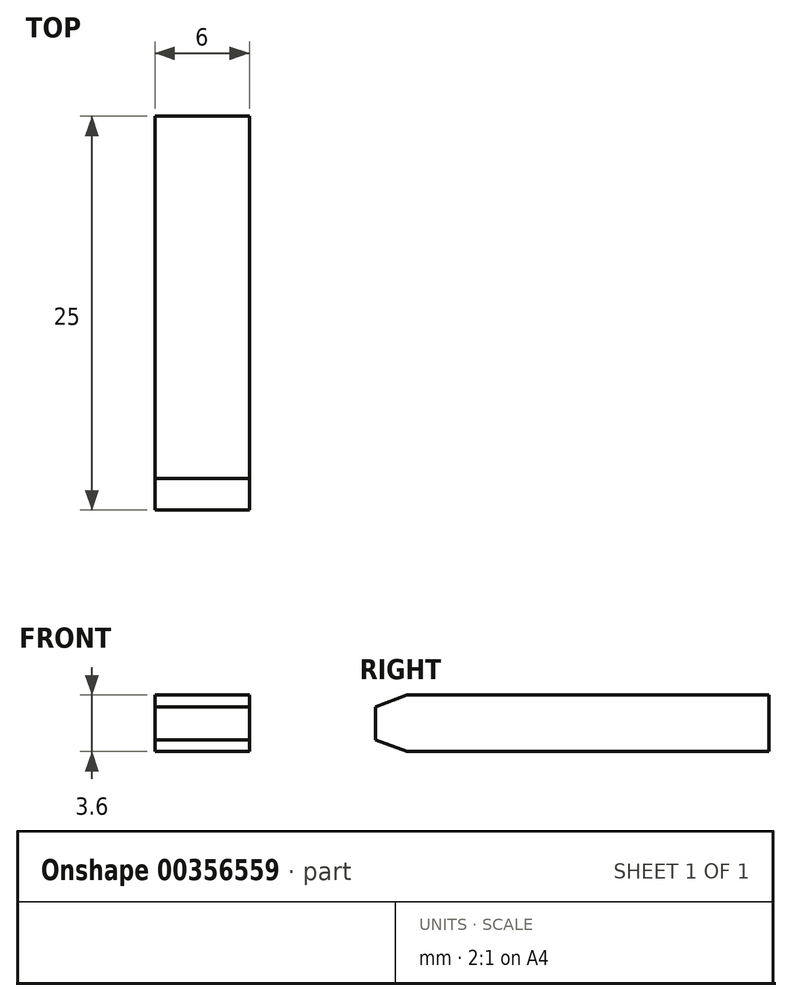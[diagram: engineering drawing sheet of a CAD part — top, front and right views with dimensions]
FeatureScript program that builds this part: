
annotation { "Feature Type Name" : "Feature", "Feature Type Description" : "" }
export const myFeature = defineFeature(function(context is Context, id is Id, definition is map)
    precondition{}
    {
        {
            var Q0;
            Q0=qCreatedBy(makeId("Front.planeOp"),FACE);
            var sketch = newSketch(context, id + "F0", { "sketchPlane" : qUnion([Q0])});
            skLineSegment(sketch, "E0.bottom", {"start": v(-4.26, -0.82) * mm, "end": v(1.74, -0.82) * mm});
            skLineSegment(sketch, "E0.top", {"start": v(-4.26, -4.42) * mm, "end": v(1.74, -4.42) * mm});
            skLineSegment(sketch, "E0.left", {"start": v(-4.26, -0.82) * mm, "end": v(-4.26, -4.42) * mm});
            skLineSegment(sketch, "E0.right", {"start": v(1.74, -0.82) * mm, "end": v(1.74, -4.42) * mm});
            skSolve(sketch);
        }
        {
            var Q0;
            Q0=makeQuery(id+"F0.imprint","IMPRINT",FACE,{"disambiguationData":[TD([[makeQuery(id+"F0.imprint","IMPRINT",EDGE,{"derivedFrom":sQuery(id+"F0.wireOp",EDGE,"E0.bottom")}),-1.0]])]});
            extrude(context, id + "F1", {"entities" : qUnion([Q0]), "depth" : 25 * mm});
        }
        {
            var Q0;
            Q0=makeQuery(id+"F1.opExtrude","CAP_EDGE",EDGE,{"disambiguationData":[OSD([sQuery(id+"F0.wireOp",EDGE,"E0.bottom")])],"isStart":false});
            var Q1;
            Q1=makeQuery(id+"F1.opExtrude","CAP_EDGE",EDGE,{"disambiguationData":[OSD([sQuery(id+"F0.wireOp",EDGE,"E0.top")])],"isStart":false});
            chamfer(context, id + "F2", {"entities" : qUnion([Q0, Q1]), "chamferType" : ChamferType.TWO_OFFSETS, "width1" : 2 * mm, "oppositeDirection" : false, "width2" : 0.75 * mm, "tangentPropagation" : true});
        }
    });
